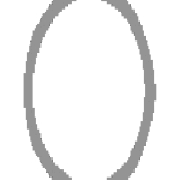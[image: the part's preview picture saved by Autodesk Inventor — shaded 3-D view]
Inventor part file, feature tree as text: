
AUTODESK INVENTOR PART (.ipt)
format: ipt  version: 2021 (Build 250183000, 183)  size: 113,664 bytes
history: native  units: in
note: dims shown in document units (in); Inventor stores cm internally (conversion verified against a paired STEP export)
features: other x4, sketch x3, plane x1
ambient origin geometry x8: Origin, YZ Plane, XZ Plane, XY Plane, X Axis, Y Axis, Z Axis, Center Point
bodies: Solid1 (feature_tree), Body (feature_tree)
feature tree (8):
  other  "Driven Length"
  other  "Frame Generator"
  other  "Start Plane"
  other  "End Plane"
  sketch  "Sketch"  dims[d2=3.0in d4=-0.0in d5=3.0in d6=0.12in d7=0.0in d8=90.0deg d9=3.0in]
  sketch  "Sketch2"  dims[d0=1.0in]
  plane  "Work Plane3"
  sketch  "Sketch3"  dims[d1=0.065in]
